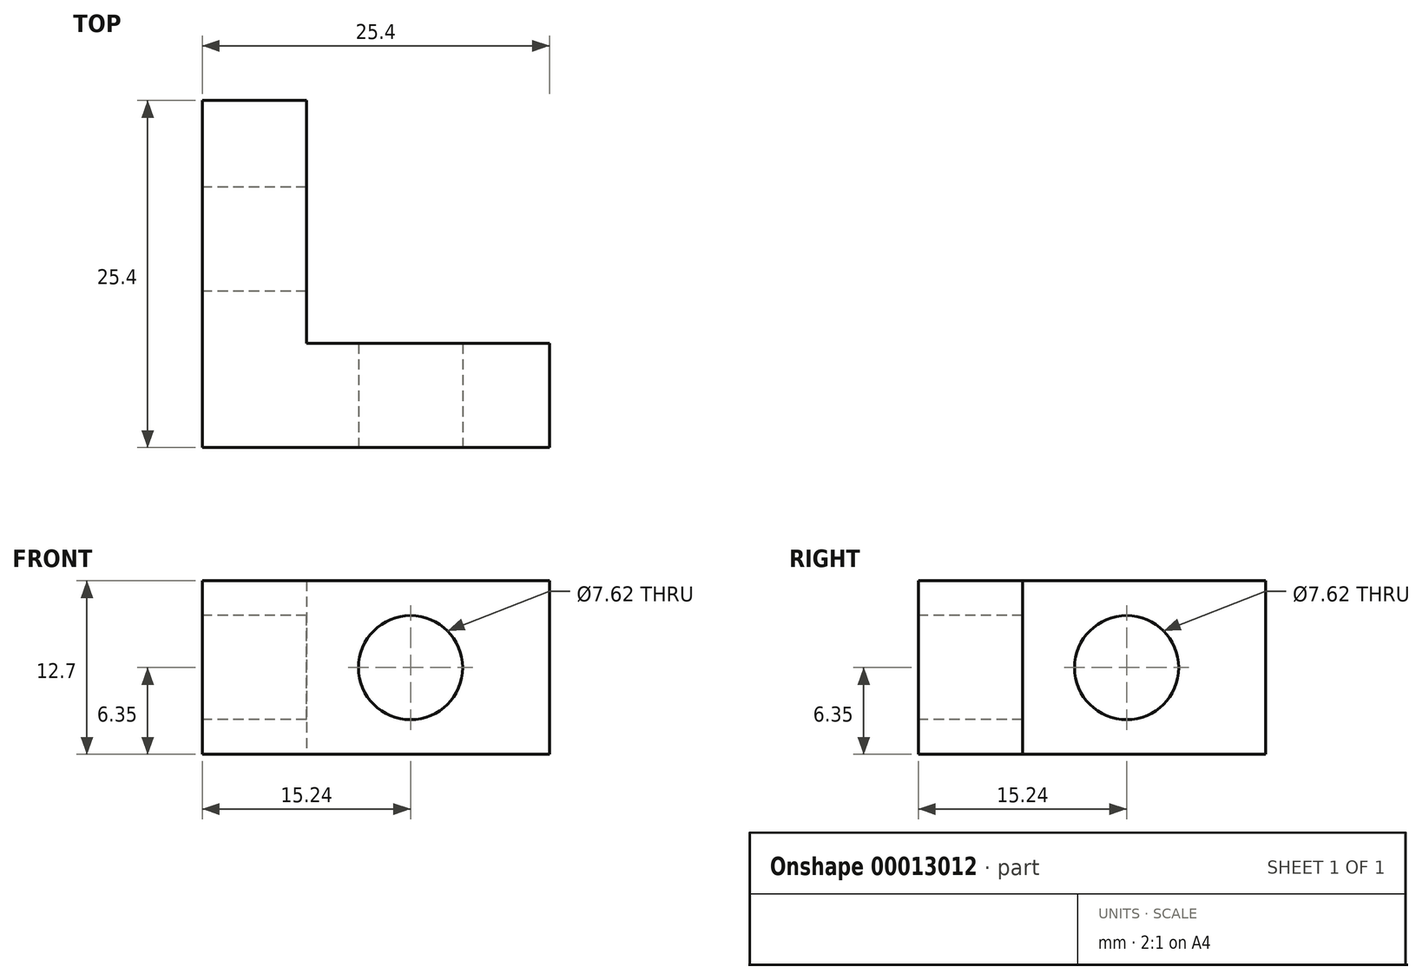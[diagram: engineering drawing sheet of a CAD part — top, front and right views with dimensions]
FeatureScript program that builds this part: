
annotation { "Feature Type Name" : "Feature", "Feature Type Description" : "" }
export const myFeature = defineFeature(function(context is Context, id is Id, definition is map)
    precondition{}
    {
        {
            var Q0;
            Q0=qCreatedBy(makeId("Top.planeOp"),FACE);
            var sketch = newSketch(context, id + "F0", { "sketchPlane" : qUnion([Q0])});
            skLineSegment(sketch, "E0", {"start": v(0, 0) * mm, "end": v(25.4, 0) * mm});
            skLineSegment(sketch, "E1", {"start": v(25.4, 0) * mm, "end": v(25.4, 7.62) * mm});
            skLineSegment(sketch, "E2", {"start": v(25.4, 7.62) * mm, "end": v(7.62, 7.62) * mm});
            skLineSegment(sketch, "E3", {"start": v(7.62, 25.4) * mm, "end": v(7.62, 7.62) * mm});
            skLineSegment(sketch, "E4", {"start": v(7.62, 25.4) * mm, "end": v(0, 25.4) * mm});
            skLineSegment(sketch, "E5", {"start": v(0, 25.4) * mm, "end": v(0, 0) * mm});
            skSolve(sketch);
        }
        {
            var Q0;
            Q0=makeQuery(id+"F0.imprint","IMPRINT",FACE,{"disambiguationData":[TD([[makeQuery(id+"F0.imprint","IMPRINT",EDGE,{"derivedFrom":sQuery(id+"F0.wireOp",EDGE,"E0")}),1.0]])]});
            extrude(context, id + "F1", {"entities" : qUnion([Q0]), "depth" : 12.7 * mm});
        }
        {
            var Q0;
            Q0=makeQuery(id+"F1.opExtrude","SWEPT_FACE",FACE,{"disambiguationData":[OSD([sQuery(id+"F0.wireOp",EDGE,"E0")])]});
            var sketch = newSketch(context, id + "F2", { "sketchPlane" : qUnion([Q0])});
            skLineSegment(sketch, "E6", {"start": v(15.24, 12.7) * mm, "end": v(15.24, 0) * mm, "construction": true});
            skCircle(sketch, "E7", {"center": v(15.24, 6.35) * mm, "radius": 3.81 * mm});
            skSolve(sketch);
        }
        {
            var Q0;
            Q0 = qSketchRegion(id + "F2", true);
            extrude(context, id + "F4", {"entities" : qUnion([Q0]), "operationType" : NewBodyOperationType.REMOVE, "endBound" : BoundingType.THROUGH_ALL, "oppositeDirection" : true, "depth" : 25.4 * mm});
        }
        {
            var Q0;
            Q0=makeQuery(id+"F1.opExtrude","SWEPT_FACE",FACE,{"disambiguationData":[OSD([sQuery(id+"F0.wireOp",EDGE,"E5")])]});
            var sketch = newSketch(context, id + "F5", { "sketchPlane" : qUnion([Q0])});
            skLineSegment(sketch, "E8", {"start": v(-15.24, 12.7) * mm, "end": v(-15.24, 0) * mm, "construction": true});
            skCircle(sketch, "E9", {"center": v(-15.24, 6.35) * mm, "radius": 3.81 * mm});
            skSolve(sketch);
        }
        {
            var Q0;
            Q0 = qSketchRegion(id + "F5", true);
            extrude(context, id + "F3", {"entities" : qUnion([Q0]), "operationType" : NewBodyOperationType.REMOVE, "endBound" : BoundingType.THROUGH_ALL, "oppositeDirection" : true, "depth" : 25.4 * mm});
        }
    });
